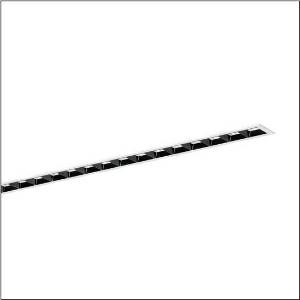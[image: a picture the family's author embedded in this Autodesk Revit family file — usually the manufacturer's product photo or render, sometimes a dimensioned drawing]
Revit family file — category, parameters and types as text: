
# Revit family: silica_r__21_51mx11dc3awb_9b11
name_source: partatom
category: Lighting Fixtures
units: mm (PartAtom-declared; Revit-internal decimal feet)

## family parameters
Cut with Voids When Loaded = No
Host = Face
Light Source = No
Part Type = Normal
Room Calculation Point = No
Round Connector Dimension = Use Diameter
Shared = No

## types (1)
- --- (1 x LED, 10800 lm, 69.3 W, 3000K)
    Apparent Load = 69 VA
    CIE Flux Codes = 87 99 100 100 100
    Color Rendering = 80
    Color Temperature = 3000K
    Default Elevation = 1800 mm
    Description = Silica® 21, office luminaire, primary light control with darklight reflector, of PMMA, black, CAT 2 (L<= 3000cd/m²), light emission: direct distribution, primary light characteristic: symmetric, installation type: recessed, LED, rated luminous flux: 10.800lm, luminous efficacy: 156lm/W, light colour: 830, colour temperature: 3000K, control gear: DALI 2, with terminal, 3+2-pole, max. 2.5mm², mains connection: 220..240V, AC, 50/60Hz, luminaire housing, of aluminium, traffic white (RAL 9016), length: 3.028mm, width: 79mm, height: 53mm, protection rating (complete): IP20, insulation class (complete): insulation class I (protective earthing), certification: CE, ENEC, VDE, permissible operating ambient temperature: 0..+35°C, standard: EN 50419, packaging unit: 1 piece
    Height = 0 mm  [stored 0 ft]
    Lamp = 1 x LED
    Lamp Light Flux = 10800 lm
    Lamp Power = 69.3 W
    Lamp count = 1
    Length = 3027 mm
    Luminous efficacy = 156 lm/W
    Manufacturer = Siteco
    ModVariant = No
    Model = 51MX11DC3AWB
    Mounting Place = Ceiling
    Mounting Type = Recessed
    Number of Poles = 1
    OnlyDefault = Yes
    Power Factor = 1
    Product Name = Silica® 21
    Product group = office luminaire | ceiling recessed
    ProductGroupID = 401
    Protection Class = Protection class I
    Protection Degree = IP 20
    RLX_Detail_Level = 1
    RLX_Emergency_Light_Flux = 0 lm
    RLX_Emergency_Type = 0
    RLX_Emergency_Type_DB = No
    RlxData = <blob elided: 62669 chars, md5=03f82d38>
    Socket = socket
    Standby Power = 0 W
    System Light Flux = 10800 lm
    System Power = 69 W
    Type Comments = factory setting: luminous flux: 100 % | dim-lin: 254 | 393 mA
    Type Image = l_1335880.jpg
    URL = http://relux.com
    VarID = @adj_123328
    Voltage = 0 V
    Weight = 0.00 kg
    Width = 79 mm

note: [stored X ft] marks values corroborated as IEEE doubles in the binary element streams (Revit-internal decimal feet)

## geometry (parser evidence)
native form markers: Blend x4, Sweep x9
no freeform markers — native parametric forms only
